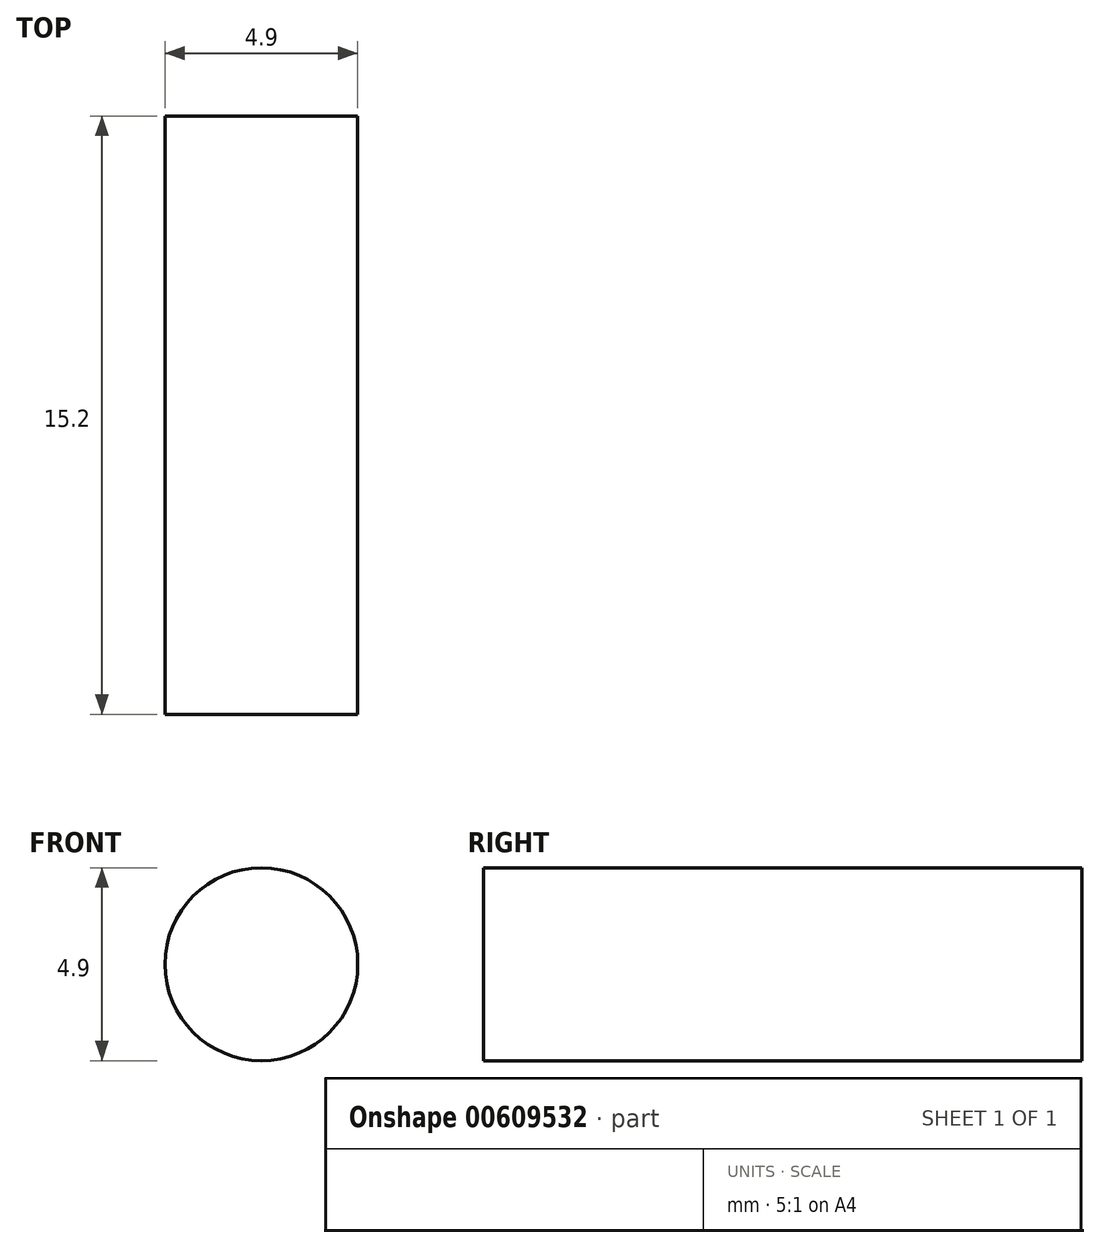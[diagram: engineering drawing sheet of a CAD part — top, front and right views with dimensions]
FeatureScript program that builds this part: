
annotation { "Feature Type Name" : "Feature", "Feature Type Description" : "" }
export const myFeature = defineFeature(function(context is Context, id is Id, definition is map)
    precondition{}
    {
        {
            var Q0;
            Q0=qCreatedBy(makeId("Top.planeOp"),FACE);
            var sketch = newSketch(context, id + "F0", { "sketchPlane" : qUnion([Q0])});
            skLineSegment(sketch, "E0.bottom", {"start": v(0, 0) * mm, "end": v(76, 0) * mm});
            skLineSegment(sketch, "E0.top", {"start": v(0, 15.2) * mm, "end": v(76, 15.2) * mm});
            skLineSegment(sketch, "E0.right", {"start": v(76, 0) * mm, "end": v(76, 15.2) * mm});
            skLineSegment(sketch, "E1.bottom", {"start": v(76, 0) * mm, "end": v(106, 0) * mm});
            skLineSegment(sketch, "E1.top", {"start": v(76, 5) * mm, "end": v(106, 5) * mm});
            skLineSegment(sketch, "E1.left", {"start": v(76, 0) * mm, "end": v(76, 5) * mm});
            skLineSegment(sketch, "E1.right", {"start": v(106, 0) * mm, "end": v(106, 5) * mm});
            skLineSegment(sketch, "E2.bottom", {"start": v(76, 15.2) * mm, "end": v(76, 15.2) * mm});
            skLineSegment(sketch, "E2.top", {"start": v(76, 10.2) * mm, "end": v(76, 10.2) * mm});
            skLineSegment(sketch, "E2.left", {"start": v(76, 15.2) * mm, "end": v(76, 10.2) * mm});
            skLineSegment(sketch, "E2.right", {"start": v(76, 15.2) * mm, "end": v(76, 10.2) * mm});
            skLineSegment(sketch, "E3.bottom", {"start": v(76, 15.2) * mm, "end": v(106, 15.2) * mm});
            skLineSegment(sketch, "E3.top", {"start": v(76, 10.2) * mm, "end": v(106, 10.2) * mm});
            skLineSegment(sketch, "E3.right", {"start": v(106, 15.2) * mm, "end": v(106, 10.2) * mm});
            skLineSegment(sketch, "E4.left", {"start": v(0, 15.2) * mm, "end": v(0, 0) * mm});
            skLineSegment(sketch, "E4.right", {"start": v(76, 15.2) * mm, "end": v(76, 0) * mm});
            skSolve(sketch);
        }
        {
            var Q0;
            {var subQ1=sQuery(id+"F0.wireOp",EDGE,"E0.top");Q0=makeQuery(id+"F0.imprint","IMPRINT",FACE,{"disambiguationData":[TD([[makeQuery(id+"F0.imprint","IMPRINT",EDGE,{"derivedFrom":subQ1}),-1.0]])]});}
            var Q1;
            {var subQ0=sQuery(id+"F0.wireOp",EDGE,"E3.bottom");Q1=makeQuery(id+"F0.imprint","IMPRINT",FACE,{"disambiguationData":[TD([[makeQuery(id+"F0.imprint","IMPRINT",EDGE,{"derivedFrom":subQ0}),-1.0]])]});}
            var Q2;
            {var subQ0=sQuery(id+"F0.wireOp",EDGE,"E1.bottom");Q2=makeQuery(id+"F0.imprint","IMPRINT",FACE,{"disambiguationData":[TD([[makeQuery(id+"F0.imprint","IMPRINT",EDGE,{"derivedFrom":subQ0}),1.0]])]});}
            extrude(context, id + "F1", {"entities" : qUnion([Q0, Q1, Q2]), "depth" : 40 * mm, "offsetDistance" : 25 * mm});
        }
        {
            var Q0;
            Q0=makeQuery(id+"F1.opExtrude","SWEPT_FACE",FACE,{"disambiguationData":[OSD([sQuery(id+"F0.wireOp",EDGE,"E1.bottom"),sQuery(id+"F0.wireOp",EDGE,"E0.bottom")])]});
            var sketch = newSketch(context, id + "F2", { "sketchPlane" : qUnion([Q0])});
            skLineSegment(sketch, "E5", {"start": v(0, 40) * mm, "end": v(3.5, 40) * mm});
            skLineSegment(sketch, "E6", {"start": v(3.5, 40) * mm, "end": v(3.5, 0) * mm});
            skPoint(sketch, "E7", {"position": v(3.5, 20) * mm});
            skCircle(sketch, "E8", {"center": v(3.5, 20) * mm, "radius": 2.45 * mm});
            skSolve(sketch);
        }
        {
            var Q0;
            {var subQ0=sQuery(id+"F2.wireOp",EDGE,"E8");var subQ1=sQuery(id+"F2.wireOp",EDGE,"E6");var subQ2=makeQuery(id+"F2.imprint","INTERSECT",VERTEX,{"disambiguationData":[OD(0.0)],"derivedFrom":[subQ1,subQ0]});Q0=makeQuery(id+"F2.imprint","IMPRINT",FACE,{"disambiguationData":[TD([[makeQuery(id+"F2.imprint","IMPRINT",EDGE,{"disambiguationData":[TD([[subQ2,-1.0]])],"derivedFrom":subQ1}),1.0]])]});}
            var Q1;
            {var subQ0=sQuery(id+"F2.wireOp",EDGE,"E8");var subQ1=sQuery(id+"F2.wireOp",EDGE,"E6");var subQ2=makeQuery(id+"F2.imprint","INTERSECT",VERTEX,{"disambiguationData":[OD(0.0)],"derivedFrom":[subQ1,subQ0]});Q1=makeQuery(id+"F2.imprint","IMPRINT",FACE,{"disambiguationData":[TD([[makeQuery(id+"F2.imprint","IMPRINT",EDGE,{"disambiguationData":[TD([[subQ2,-1.0]])],"derivedFrom":subQ1}),-1.0]])]});}
            var Q2;
            Q2=sQuery(id+"F2.wireOp",EDGE,"E8");
            extrude(context, id + "F3", {"entities" : qUnion([Q0, Q1]), "operationType" : NewBodyOperationType.REMOVE, "surfaceEntities" : qUnion([Q2]), "oppositeDirection" : true, "depth" : 25 * mm, "offsetDistance" : 25 * mm});
        }
    });
